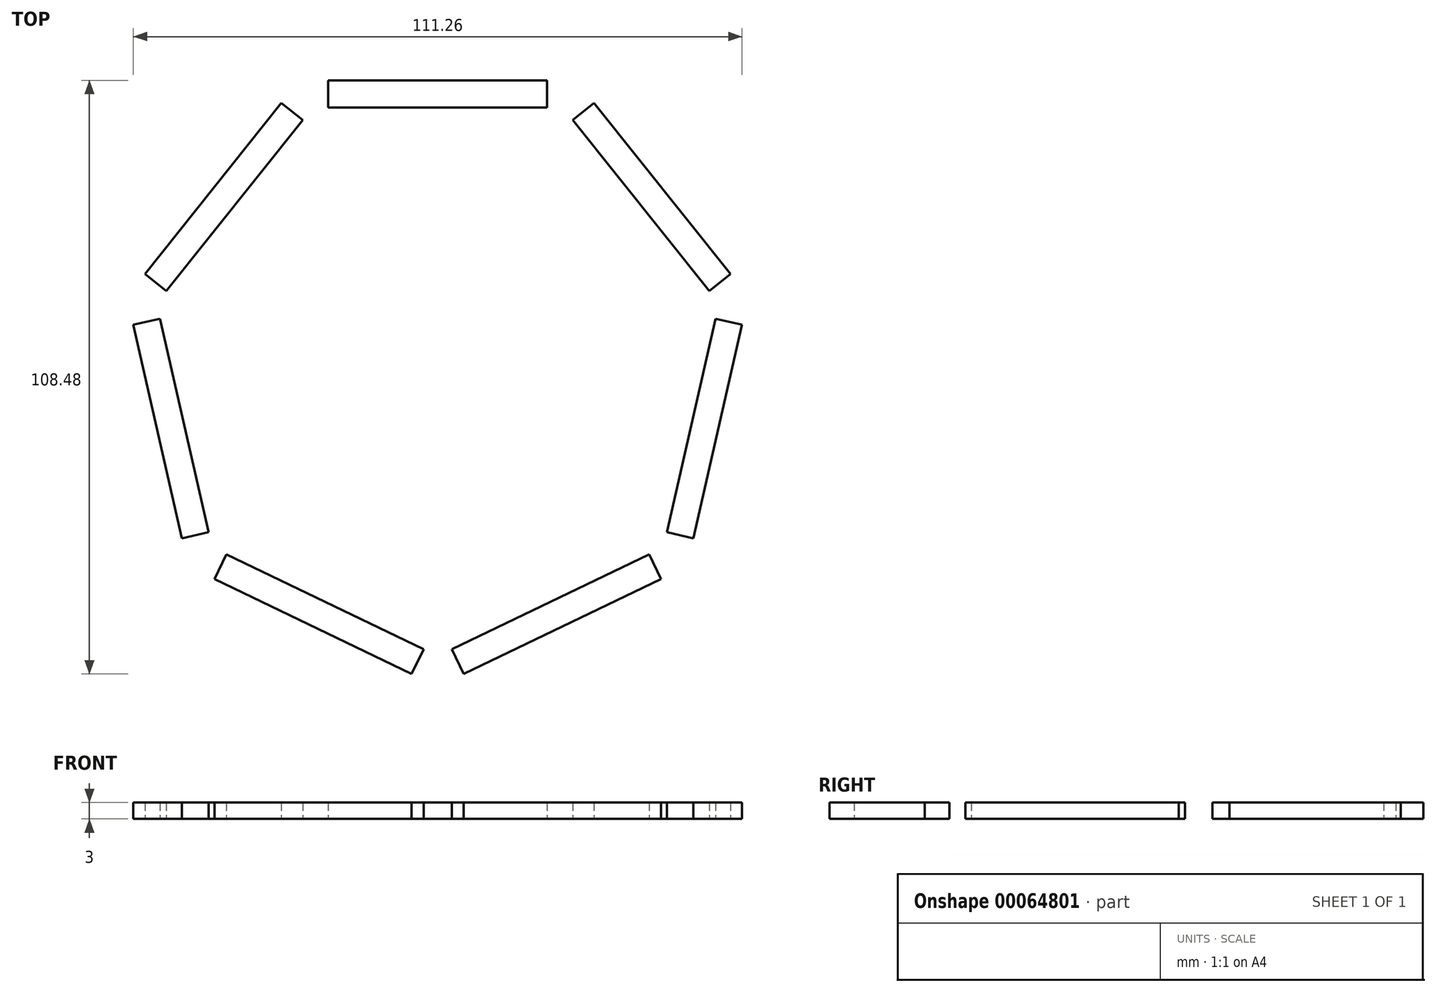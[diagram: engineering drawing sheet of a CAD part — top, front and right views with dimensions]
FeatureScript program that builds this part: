
annotation { "Feature Type Name" : "Feature", "Feature Type Description" : "" }
export const myFeature = defineFeature(function(context is Context, id is Id, definition is map)
    precondition{}
    {
        {
            var Q0;
            Q0=qCreatedBy(makeId("Top.planeOp"),FACE);
            var sketch = newSketch(context, id + "F0", { "sketchPlane" : qUnion([Q0])});
            skLineSegment(sketch, "E0.rect.bottom", {"start": v(20, 47.5) * mm, "end": v(-20, 47.5) * mm});
            skLineSegment(sketch, "E0.rect.top", {"start": v(20, 52.5) * mm, "end": v(-20, 52.5) * mm});
            skLineSegment(sketch, "E0.rect.left", {"start": v(20, 47.5) * mm, "end": v(20, 52.5) * mm});
            skLineSegment(sketch, "E0.rect.right", {"start": v(-20, 47.5) * mm, "end": v(-20, 52.5) * mm});
            skPoint(sketch, "E0.rect.middle", {"position": v(0, 50) * mm});
            skPoint(sketch, "E1.1.0", {"position": v(-39.1, 31.17) * mm});
            skLineSegment(sketch, "E1.1.1", {"start": v(-24.67, 45.25) * mm, "end": v(-49.6, 13.98) * mm});
            skLineSegment(sketch, "E1.1.2", {"start": v(-24.67, 45.25) * mm, "end": v(-28.58, 48.37) * mm});
            skLineSegment(sketch, "E1.1.3", {"start": v(-28.58, 48.37) * mm, "end": v(-53.52, 17.1) * mm});
            skLineSegment(sketch, "E1.1.4", {"start": v(-49.6, 13.98) * mm, "end": v(-53.52, 17.1) * mm});
            skPoint(sketch, "E1.2.0", {"position": v(-48.75, -11.13) * mm});
            skLineSegment(sketch, "E1.2.1", {"start": v(-50.76, 8.93) * mm, "end": v(-41.86, -30.07) * mm});
            skLineSegment(sketch, "E1.2.2", {"start": v(-50.76, 8.93) * mm, "end": v(-55.63, 7.82) * mm});
            skLineSegment(sketch, "E1.2.3", {"start": v(-55.63, 7.82) * mm, "end": v(-46.73, -31.18) * mm});
            skLineSegment(sketch, "E1.2.4", {"start": v(-41.86, -30.07) * mm, "end": v(-46.73, -31.18) * mm});
            skPoint(sketch, "E1.center", {"position": v(0, 0) * mm});
            skPoint(sketch, "E2.0.3.0", {"position": v(-21.7, -45.05) * mm});
            skLineSegment(sketch, "E2.1.3.0", {"start": v(-38.63, -34.12) * mm, "end": v(-2.6, -51.47) * mm});
            skLineSegment(sketch, "E2.4.3.0", {"start": v(-38.63, -34.12) * mm, "end": v(-40.8, -38.62) * mm});
            skLineSegment(sketch, "E2.7.3.0", {"start": v(-40.8, -38.62) * mm, "end": v(-4.76, -55.98) * mm});
            skLineSegment(sketch, "E2.10.3.0", {"start": v(-2.6, -51.47) * mm, "end": v(-4.76, -55.98) * mm});
            skPoint(sketch, "E2.0.4.0", {"position": v(21.7, -45.05) * mm});
            skLineSegment(sketch, "E2.1.4.0", {"start": v(2.6, -51.47) * mm, "end": v(38.63, -34.12) * mm});
            skLineSegment(sketch, "E2.4.4.0", {"start": v(2.6, -51.47) * mm, "end": v(4.76, -55.98) * mm});
            skLineSegment(sketch, "E2.7.4.0", {"start": v(4.76, -55.98) * mm, "end": v(40.8, -38.62) * mm});
            skLineSegment(sketch, "E2.10.4.0", {"start": v(38.63, -34.12) * mm, "end": v(40.8, -38.62) * mm});
            skPoint(sketch, "E2.0.5.0", {"position": v(48.75, -11.13) * mm});
            skLineSegment(sketch, "E2.1.5.0", {"start": v(41.86, -30.07) * mm, "end": v(50.76, 8.93) * mm});
            skLineSegment(sketch, "E2.4.5.0", {"start": v(41.86, -30.07) * mm, "end": v(46.73, -31.18) * mm});
            skLineSegment(sketch, "E2.7.5.0", {"start": v(46.73, -31.18) * mm, "end": v(55.63, 7.82) * mm});
            skLineSegment(sketch, "E2.10.5.0", {"start": v(50.76, 8.93) * mm, "end": v(55.63, 7.82) * mm});
            skPoint(sketch, "E3.0.6.0", {"position": v(39.1, 31.17) * mm});
            skLineSegment(sketch, "E3.1.6.0", {"start": v(49.6, 13.98) * mm, "end": v(24.67, 45.25) * mm});
            skLineSegment(sketch, "E3.4.6.0", {"start": v(49.6, 13.98) * mm, "end": v(53.52, 17.1) * mm});
            skLineSegment(sketch, "E3.7.6.0", {"start": v(53.52, 17.1) * mm, "end": v(28.58, 48.37) * mm});
            skLineSegment(sketch, "E3.10.6.0", {"start": v(24.67, 45.25) * mm, "end": v(28.58, 48.37) * mm});
            skSolve(sketch);
        }
        {
            var Q0;
            Q0 = qSketchRegion(id + "F0", true);
            extrude(context, id + "F1", {"entities" : qUnion([Q0]), "depth" : 3 * mm});
        }
    });
